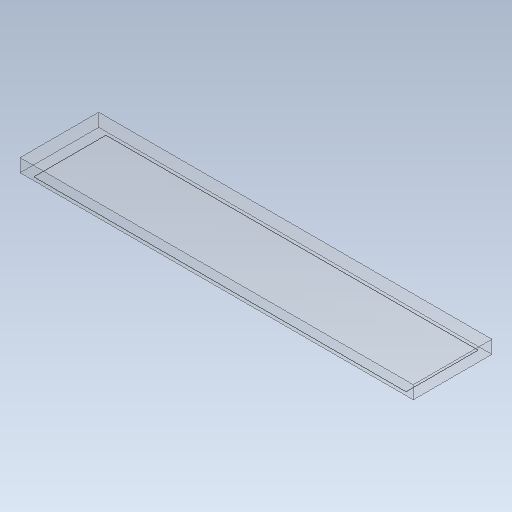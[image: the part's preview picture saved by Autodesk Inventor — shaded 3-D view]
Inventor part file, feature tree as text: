
AUTODESK INVENTOR PART (.ipt)
format: ipt  version: 2020.1 (Build 241239000, 239)  size: 113,152 bytes
history: native  units: mm
features: extrude x2, sketch x2
ambient origin geometry x8: Origin, YZ Plane, XZ Plane, XY Plane, X Axis, Y Axis, Z Axis, Center Point
bodies: Solid1 (feature_tree)
feature tree (4):
  extrude  "Extrusion1"  Depth=12.0mm
  extrude  "Extrusion2"  Depth=0.5mm
  sketch  "Sketch1"  dims[d0=60.0mm d1=12.0mm]
  sketch  "Sketch2"  dims[d2=2.0mm d3=0.0mm d4=0.5mm d5=1.6mm d6=0.02mm d7=0.0mm]
